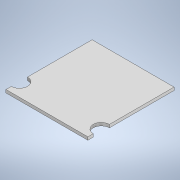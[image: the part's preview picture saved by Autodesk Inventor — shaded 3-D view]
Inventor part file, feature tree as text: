
AUTODESK INVENTOR PART (.ipt)
format: ipt  version: 2022.3 (Build 263350000, 350)  size: 103,424 bytes
history: native  units: in
note: dims shown in document units (in); Inventor stores cm internally (conversion verified against a paired STEP export)
features: extrude x1, sketch x1
ambient origin geometry x8: Origin, YZ Plane, XZ Plane, XY Plane, X Axis, Y Axis, Z Axis, Center Point
bodies: Solid1 (feature_tree)
feature tree (2):
  extrude  "Extrusion1"  Depth=0.1969in
  sketch  "Sketch2"  dims[d0=5.3937in d4=1.063in d6=1.063in d7=4.3307in d8=0.8858in d9=0.1969in d10=0.0in]
